# Revit family: H-200
name_source: partatom
category: Plumbing Fixtures
revit_build: Autodesk Revit 2014 (Build: 20130308_1515(x64)
units: mm (PartAtom-declared; Revit-internal decimal feet)

## types (1)
- H-200
    Brass Chromed = Brass
    Certification = http://helvex.com
    Compliance = NOM-008-CONAGUA-1998
    Data Sheet = http://helvex.com
    Description = Fixed Stream Showerhead Includes Arm And Escutcheon
    Features = Low, Medium And High Pressure Showerhead; Dynamic Water Economizer Included; Includes Mobile Node
    Inlet Threads = ½" - 14 NPT
    Instructive = http://helvex.com
    Manufacturer = HELVEX
    Max. Water Flow = 2.6 gal/min
    Max. Working Pressure = 85.3 psi
    Min. Water Flow = 1.0 gal/min
    Min. Working Pressure = 2.8 psi
    Model = H-200
    Total Length = 8"
    Total Width = 3"
    Type Comments = Showerheads
    URL = http://helvex.com

## geometry (parser evidence)
native form markers: Sweep x3
no freeform markers — native parametric forms only
